# Revit family: HD140M12G
name_source: partatom
category: Detail Items
revit_build: Autodesk Revit 2015 (Build: 20140606_1530(x64)
units: mm (PartAtom-declared; Revit-internal decimal feet)

## types (4) — shared parameters
Density = 0.64 kg
Description = Holdowns
EPD = https://www.strongtie.eu
ETA / DoP = https://www.strongtie.eu
Manufacturer = Simpson Strong-Tie
Model = HD140M12G
Model Disclaimer = Contact Simpson Strong-Tie Company  for more information
Model ID = 0028953864097107266735624742240930969867
Name = HD140M12G
ObjectType = HD140M12G
Product Material = Galvanised
Product Type = Holdowns
Reference = HD140M12G
Technical datasheet = https://www.strongtie.eu
URL = www.strongtie.eu
UniClass Number = Pr_20_29_31_13
UniClass Title = Carbon steel punched metal plate fasteners

## per-type parameters (varying)
| type | _visiblefront | _visibleleft | _visibleright | _visibletop |
| SST_HD140M12G_Top | No | No | No | Yes |
| SST_HD140M12G_Front | Yes | No | No | No |
| SST_HD140M12G_Left | No | Yes | No | No |
| SST_HD140M12G_Right | No | No | Yes | No |

## geometry (parser evidence)
native form markers: Sweep x2
no freeform markers — native parametric forms only
